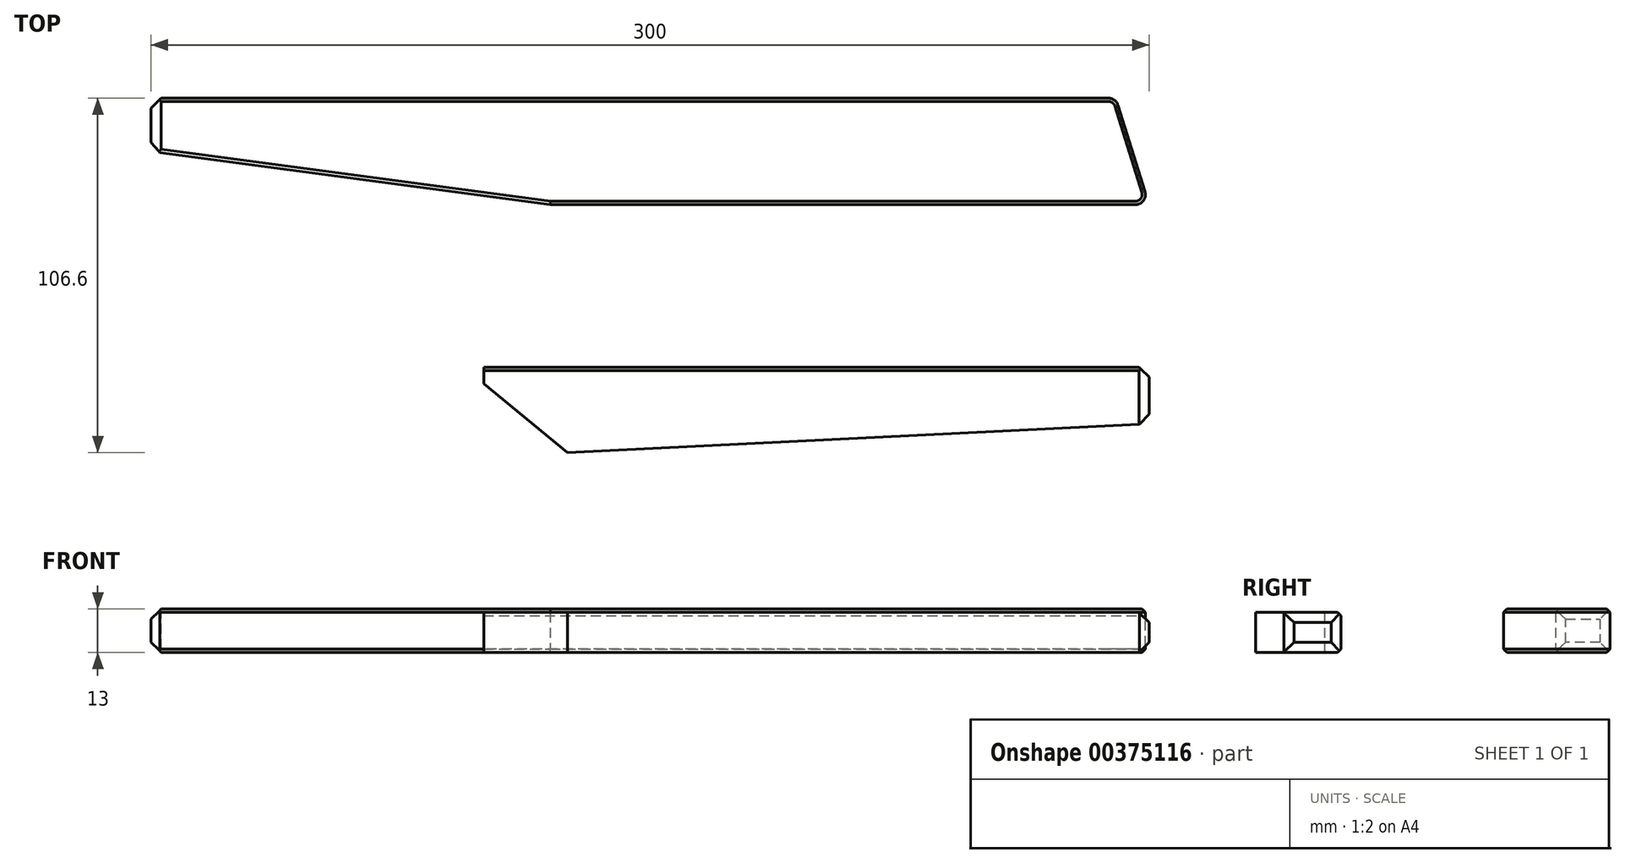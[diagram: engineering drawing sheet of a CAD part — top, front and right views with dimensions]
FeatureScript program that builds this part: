
annotation { "Feature Type Name" : "Feature", "Feature Type Description" : "" }
export const myFeature = defineFeature(function(context is Context, id is Id, definition is map)
    precondition{}
    {
        {
            var Q0;
            Q0=qCreatedBy(makeId("Top.planeOp"),FACE);
            var sketch = newSketch(context, id + "F0", { "sketchPlane" : qUnion([Q0])});
            skLineSegment(sketch, "E0", {"start": v(0, 0) * mm, "end": v(0, 32) * mm, "construction": true});
            skLineSegment(sketch, "E1", {"start": v(0, 32) * mm, "end": v(-300, 32) * mm, "construction": true});
            skLineSegment(sketch, "E2", {"start": v(-300, 32) * mm, "end": v(-300, 16) * mm, "construction": true});
            skLineSegment(sketch, "E3", {"start": v(0, 0) * mm, "end": v(-180, 0) * mm, "construction": true});
            skLineSegment(sketch, "E4", {"start": v(-180, 0) * mm, "end": v(-300, 16) * mm, "construction": true});
            skLineSegment(sketch, "E5", {"start": v(0, 32) * mm, "end": v(-10, 32) * mm, "construction": true});
            skLineSegment(sketch, "E6", {"start": v(0, 0) * mm, "end": v(-10, 32) * mm});
            skLineSegment(sketch, "E7", {"start": v(-300, 32) * mm, "end": v(-10, 32) * mm});
            skLineSegment(sketch, "E8", {"start": v(0, 0) * mm, "end": v(-180, 0) * mm});
            skLineSegment(sketch, "E9", {"start": v(-180, 0) * mm, "end": v(-300, 16) * mm});
            skLineSegment(sketch, "E10", {"start": v(-300, 16) * mm, "end": v(-300, 32) * mm});
            skSolve(sketch);
        }
        {
            var Q0;
            Q0=makeQuery(id+"F0.imprint","IMPRINT",FACE,{"disambiguationData":[TD([[makeQuery(id+"F0.imprint","IMPRINT",EDGE,{"derivedFrom":sQuery(id+"F0.wireOp",EDGE,"E6")}),1.0]])]});
            extrude(context, id + "F1", {"entities" : qUnion([Q0]), "depth" : 13 * mm});
        }
        {
            var Q0;
            Q0=makeQuery(id+"F1.opExtrude","SWEPT_EDGE",EDGE,{"disambiguationData":[OSD([sQuery(id+"F0.wireOp",EDGE,"E6"),sQuery(id+"F0.wireOp",EDGE,"E7")])]});
            var Q1;
            Q1=makeQuery(id+"F1.opExtrude","SWEPT_EDGE",EDGE,{"disambiguationData":[OSD([sQuery(id+"F0.wireOp",EDGE,"E6"),sQuery(id+"F0.wireOp",EDGE,"E8")])]});
            fillet(context, id + "F2", {"entities" : qUnion([Q0, Q1]), "radius" : 3 * mm, "tangentPropagation" : true, "allowEdgeOverflow" : false});
        }
        {
            var Q0;
            Q0=makeQuery(id+"F1.opExtrude","CAP_EDGE",EDGE,{"disambiguationData":[OSD([sQuery(id+"F0.wireOp",EDGE,"E10")])],"isStart":false});
            var Q1;
            Q1=makeQuery(id+"F1.opExtrude","CAP_EDGE",EDGE,{"disambiguationData":[OSD([sQuery(id+"F0.wireOp",EDGE,"E10")])],"isStart":true});
            var Q2;
            Q2=makeQuery(id+"F1.opExtrude","SWEPT_EDGE",EDGE,{"disambiguationData":[OSD([sQuery(id+"F0.wireOp",EDGE,"E7"),sQuery(id+"F0.wireOp",EDGE,"E10")])]});
            var Q3;
            Q3=makeQuery(id+"F1.opExtrude","SWEPT_EDGE",EDGE,{"disambiguationData":[OSD([sQuery(id+"F0.wireOp",EDGE,"E9"),sQuery(id+"F0.wireOp",EDGE,"E10")])]});
            chamfer(context, id + "F3", {"entities" : qUnion([Q0, Q1, Q2, Q3]), "width" : 3 * mm, "tangentPropagation" : true});
        }
        {
            var Q0;
            Q0=makeQuery(id+"F1.opExtrude","CAP_EDGE",EDGE,{"disambiguationData":[OSD([sQuery(id+"F0.wireOp",EDGE,"E7")])],"isStart":false});
            var Q1;
            Q1=makeQuery(id+"F1.opExtrude","CAP_EDGE",EDGE,{"disambiguationData":[OSD([sQuery(id+"F0.wireOp",EDGE,"E7")])],"isStart":true});
            var Q2;
            Q2=makeQuery(id+"F1.opExtrude","CAP_EDGE",EDGE,{"disambiguationData":[OSD([sQuery(id+"F0.wireOp",EDGE,"E9")])],"isStart":false});
            var Q3;
            Q3=makeQuery(id+"F1.opExtrude","CAP_EDGE",EDGE,{"disambiguationData":[OSD([sQuery(id+"F0.wireOp",EDGE,"E8")])],"isStart":false});
            var Q4;
            Q4=makeQuery(id+"F1.opExtrude","CAP_EDGE",EDGE,{"disambiguationData":[OSD([sQuery(id+"F0.wireOp",EDGE,"E9")])],"isStart":true});
            var Q5;
            Q5=makeQuery(id+"F1.opExtrude","CAP_EDGE",EDGE,{"disambiguationData":[OSD([sQuery(id+"F0.wireOp",EDGE,"E8")])],"isStart":true});
            chamfer(context, id + "F4", {"entities" : qUnion([Q0, Q1, Q2, Q3, Q4, Q5]), "width" : 1 * mm, "tangentPropagation" : true});
        }
        {
            var Q0;
            Q0=qCreatedBy(makeId("Top.planeOp"),FACE);
            var sketch = newSketch(context, id + "F5", { "sketchPlane" : qUnion([Q0])});
            skLineSegment(sketch, "E11", {"start": v(0, -48.86) * mm, "end": v(0, -65.86) * mm, "construction": true});
            skLineSegment(sketch, "E12", {"start": v(0, -48.86) * mm, "end": v(-200, -48.86) * mm, "construction": true});
            skLineSegment(sketch, "E13", {"start": v(-200, -48.86) * mm, "end": v(-200, -53.86) * mm, "construction": true});
            skLineSegment(sketch, "E14", {"start": v(-200, -48.86) * mm, "end": v(-200, -75.86) * mm, "construction": true});
            skPoint(sketch, "E14.endSnap0", {"position": v(-200, -51.36) * mm});
            skLineSegment(sketch, "E15", {"start": v(-200, -75.86) * mm, "end": v(0, -65.86) * mm, "construction": true});
            skLineSegment(sketch, "E16", {"start": v(0, -65.86) * mm, "end": v(-174.78, -74.6) * mm});
            skLineSegment(sketch, "E17", {"start": v(-174.78, -74.6) * mm, "end": v(-200, -53.86) * mm});
            skLineSegment(sketch, "E18", {"start": v(-200, -48.86) * mm, "end": v(0, -48.86) * mm});
            skLineSegment(sketch, "E19", {"start": v(-200, -53.86) * mm, "end": v(-200, -48.86) * mm});
            skLineSegment(sketch, "E20", {"start": v(0, -48.86) * mm, "end": v(0, -65.86) * mm});
            skSolve(sketch);
        }
        {
            var Q0;
            Q0=makeQuery(id+"F5.imprint","IMPRINT",FACE,{"disambiguationData":[TD([[makeQuery(id+"F5.imprint","IMPRINT",EDGE,{"derivedFrom":sQuery(id+"F5.wireOp",EDGE,"E16")}),-1.0]])]});
            extrude(context, id + "F6", {"entities" : qUnion([Q0]), "depth" : 12 * mm});
        }
        {
            var Q0;
            Q0=makeQuery(id+"F6.opExtrude","CAP_EDGE",EDGE,{"disambiguationData":[OSD([sQuery(id+"F5.wireOp",EDGE,"E18")])],"isStart":false});
            var Q1;
            Q1=makeQuery(id+"F6.opExtrude","CAP_EDGE",EDGE,{"disambiguationData":[OSD([sQuery(id+"F5.wireOp",EDGE,"E18")])],"isStart":true});
            chamfer(context, id + "F7", {"entities" : qUnion([Q0, Q1]), "width" : 1 * mm, "tangentPropagation" : true});
        }
        {
            var Q0;
            Q0=makeQuery(id+"F6.opExtrude","CAP_EDGE",EDGE,{"disambiguationData":[OSD([sQuery(id+"F5.wireOp",EDGE,"E20")])],"isStart":false});
            var Q1;
            Q1=makeQuery(id+"F6.opExtrude","SWEPT_EDGE",EDGE,{"disambiguationData":[OSD([sQuery(id+"F5.wireOp",EDGE,"E18"),sQuery(id+"F5.wireOp",EDGE,"E20")])]});
            var Q2;
            Q2=makeQuery(id+"F6.opExtrude","SWEPT_EDGE",EDGE,{"disambiguationData":[OSD([sQuery(id+"F5.wireOp",EDGE,"E16"),sQuery(id+"F5.wireOp",EDGE,"E20")])]});
            var Q3;
            Q3=makeQuery(id+"F6.opExtrude","CAP_EDGE",EDGE,{"disambiguationData":[OSD([sQuery(id+"F5.wireOp",EDGE,"E20")])],"isStart":true});
            chamfer(context, id + "F8", {"entities" : qUnion([Q0, Q1, Q2, Q3]), "width" : 3 * mm, "tangentPropagation" : true});
        }
    });
